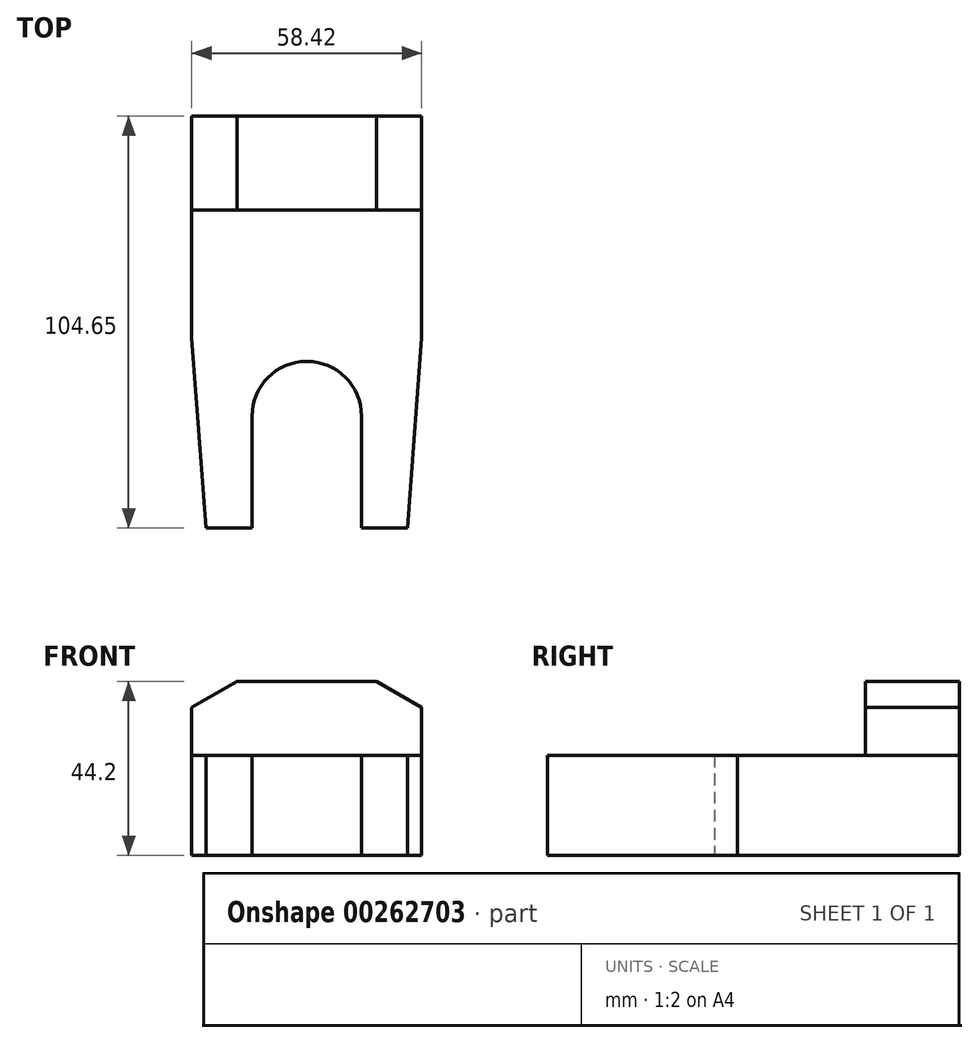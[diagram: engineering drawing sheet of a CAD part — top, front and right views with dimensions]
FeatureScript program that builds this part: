
annotation { "Feature Type Name" : "Feature", "Feature Type Description" : "" }
export const myFeature = defineFeature(function(context is Context, id is Id, definition is map)
    precondition{}
    {
        {
            var Q0;
            Q0=qCreatedBy(makeId("Top.planeOp"),FACE);
            var sketch = newSketch(context, id + "F0", { "sketchPlane" : qUnion([Q0])});
            skLineSegment(sketch, "E0.bottom", {"start": v(25.43, 26.97) * mm, "end": v(83.85, 26.97) * mm});
            skLineSegment(sketch, "E0.top", {"start": v(29.07, -77.68) * mm, "end": v(40.76, -77.68) * mm});
            skLineSegment(sketch, "E0.left", {"start": v(25.43, 26.97) * mm, "end": v(25.43, -29.42) * mm});
            skLineSegment(sketch, "E0.right", {"start": v(83.85, 26.97) * mm, "end": v(83.85, -29.42) * mm});
            skLineSegment(sketch, "E1.left", {"start": v(40.76, -49.23) * mm, "end": v(40.76, -77.68) * mm});
            skLineSegment(sketch, "E1.right", {"start": v(68.52, -49.23) * mm, "end": v(68.52, -77.68) * mm});
            skArc(sketch, "E2", {"start": v(68.52, -49.23) * mm, "mid": v(54.64, -35.35) * mm, "end": v(40.76, -49.23) * mm});
            skLineSegment(sketch, "E3", {"start": v(25.43, -29.42) * mm, "end": v(29.07, -77.68) * mm});
            skLineSegment(sketch, "E4", {"start": v(80.2, -77.68) * mm, "end": v(83.85, -29.42) * mm});
            skLineSegment(sketch, "E5.trimOffspring", {"start": v(68.52, -77.68) * mm, "end": v(80.2, -77.68) * mm});
            skSolve(sketch);
        }
        {
            var Q0;
            Q0 = qSketchRegion(id + "F0", true);
            extrude(context, id + "F1", {"entities" : qUnion([Q0]), "depth" : 25.4 * mm});
        }
        {
            var Q0;
            Q0=makeQuery(id+"F1.opExtrude","SWEPT_FACE",FACE,{"disambiguationData":[OSD([sQuery(id+"F0.wireOp",EDGE,"E0.bottom")])]});
            var sketch = newSketch(context, id + "F2", { "sketchPlane" : qUnion([Q0])});
            skLineSegment(sketch, "E6", {"start": v(-83.85, 37.6) * mm, "end": v(-83.85, 25.4) * mm});
            skLineSegment(sketch, "E7", {"start": v(-83.85, 25.4) * mm, "end": v(-25.43, 25.4) * mm});
            skLineSegment(sketch, "E8", {"start": v(-25.43, 25.4) * mm, "end": v(-25.43, 37.6) * mm});
            skLineSegment(sketch, "E9", {"start": v(-83.85, 37.6) * mm, "end": v(-72.4, 44.2) * mm});
            skLineSegment(sketch, "E10", {"start": v(-72.4, 44.2) * mm, "end": v(-36.86, 44.2) * mm});
            skLineSegment(sketch, "E11", {"start": v(-36.86, 44.2) * mm, "end": v(-25.43, 37.6) * mm});
            skSolve(sketch);
        }
        {
            var Q0;
            Q0 = qSketchRegion(id + "F2", true);
            extrude(context, id + "F3", {"entities" : qUnion([Q0]), "oppositeDirection" : true, "depth" : 23.88 * mm});
        }
    });
